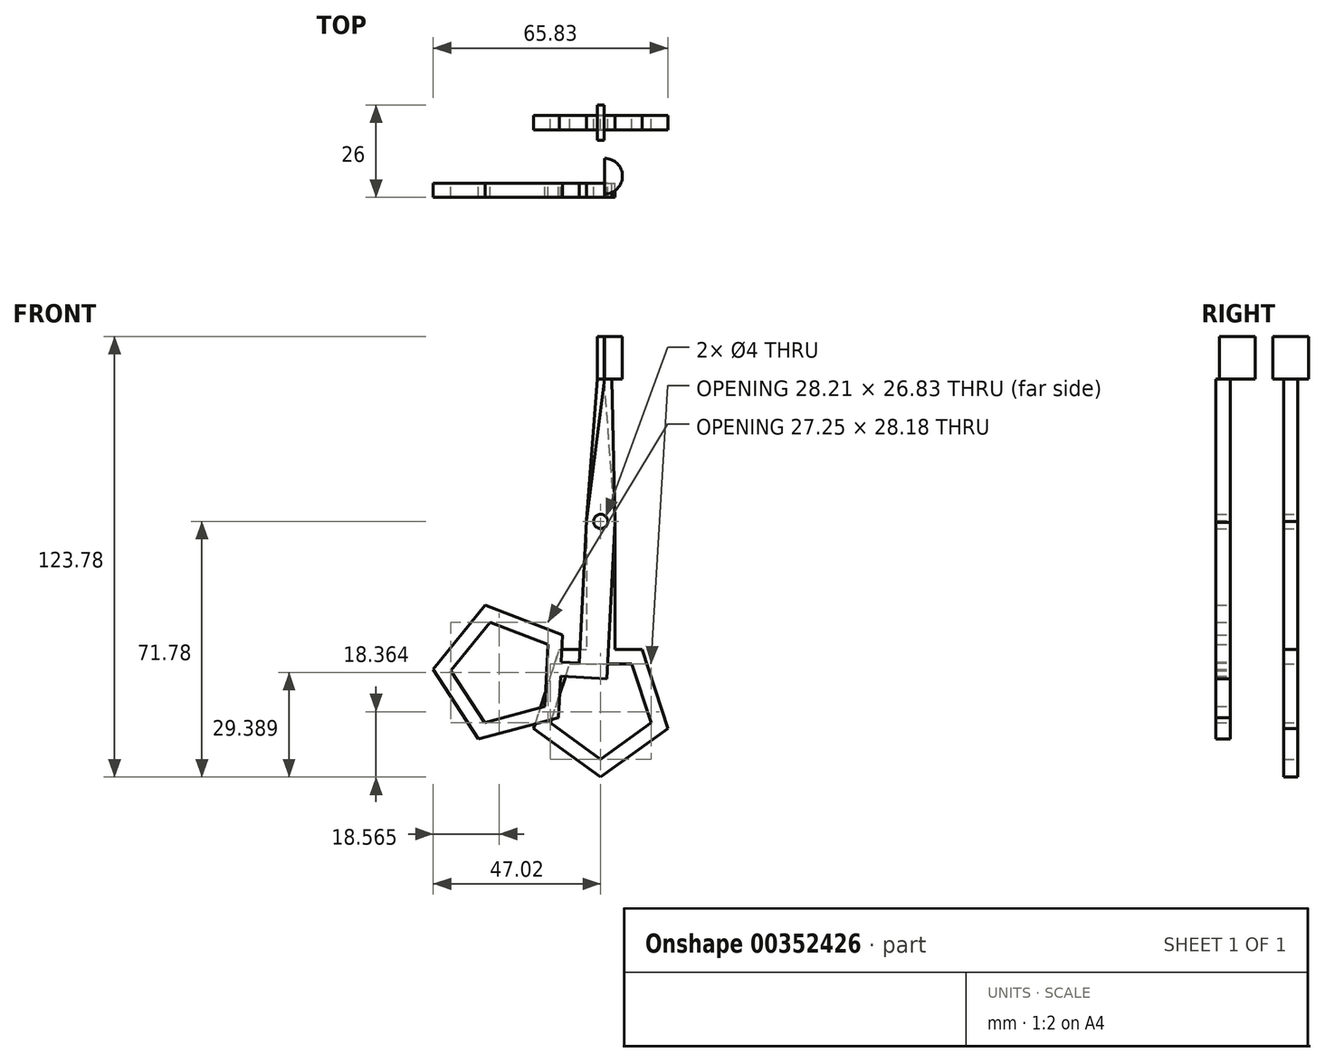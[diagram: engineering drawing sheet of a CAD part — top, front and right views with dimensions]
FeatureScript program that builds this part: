
annotation { "Feature Type Name" : "Feature", "Feature Type Description" : "" }
export const myFeature = defineFeature(function(context is Context, id is Id, definition is map)
    precondition{}
    {
        {
            var Q0;
            Q0=qCreatedBy(makeId("Front.planeOp"),FACE);
            var sketch = newSketch(context, id + "F0", { "sketchPlane" : qUnion([Q0])});
            skLineSegment(sketch, "E0.top", {"start": v(4, -40) * mm, "end": v(-4, -40) * mm});
            skLineSegment(sketch, "E0.left", {"start": v(4, 0) * mm, "end": v(4, -40) * mm});
            skLineSegment(sketch, "E0.right", {"start": v(-4, 0) * mm, "end": v(-4, -40) * mm});
            skPoint(sketch, "E0.middle", {"position": v(0, 0) * mm});
            skLineSegment(sketch, "E1", {"start": v(0, -40) * mm, "end": v(0, -52) * mm, "construction": true});
            skPoint(sketch, "E1.endSnap0", {"position": v(0, -40) * mm});
            skCircle(sketch, "E2.cCircle", {"center": v(0, -52) * mm, "radius": 12 * mm, "construction": true});
            skLineSegment(sketch, "E2.0", {"start": v(-8.72, -40) * mm, "end": v(8.72, -40) * mm});
            skLineSegment(sketch, "E2.1", {"start": v(8.72, -40) * mm, "end": v(14.1, -56.58) * mm});
            skLineSegment(sketch, "E2.2", {"start": v(14.1, -56.58) * mm, "end": v(0, -66.83) * mm});
            skLineSegment(sketch, "E2.3", {"start": v(0, -66.83) * mm, "end": v(-14.1, -56.58) * mm});
            skLineSegment(sketch, "E2.4", {"start": v(-14.1, -56.58) * mm, "end": v(-8.72, -40) * mm});
            skLineSegment(sketch, "E3", {"start": v(0, -40) * mm, "end": v(0, -36) * mm, "construction": true});
            skCircle(sketch, "E4.cCircle", {"center": v(0, -52) * mm, "radius": 16 * mm, "construction": true});
            skLineSegment(sketch, "E4.0", {"start": v(-11.62, -36) * mm, "end": v(11.62, -36) * mm});
            skLineSegment(sketch, "E4.1", {"start": v(11.62, -36) * mm, "end": v(18.8, -58.11) * mm});
            skLineSegment(sketch, "E4.2", {"start": v(18.8, -58.11) * mm, "end": v(0, -71.78) * mm});
            skLineSegment(sketch, "E4.3", {"start": v(0, -71.78) * mm, "end": v(-18.8, -58.11) * mm});
            skLineSegment(sketch, "E4.4", {"start": v(-18.8, -58.11) * mm, "end": v(-11.62, -36) * mm});
            skPoint(sketch, "E4.0.midPoint", {"position": v(0, -36) * mm});
            skLineSegment(sketch, "E5.bottom", {"start": v(-1, 40) * mm, "end": v(1, 40) * mm});
            skLineSegment(sketch, "E5.top", {"start": v(-1, 52) * mm, "end": v(1, 52) * mm});
            skLineSegment(sketch, "E5.left", {"start": v(-1, 40) * mm, "end": v(-1, 52) * mm});
            skLineSegment(sketch, "E5.right", {"start": v(1, 40) * mm, "end": v(1, 52) * mm});
            skPoint(sketch, "E6", {"position": v(0, 40) * mm});
            skCircle(sketch, "E7", {"center": v(0, 0) * mm, "radius": 2 * mm});
            skPoint(sketch, "E8", {"position": v(-4, 0) * mm});
            skPoint(sketch, "E9", {"position": v(4, 0) * mm});
            skLineSegment(sketch, "E10", {"start": v(-4, 0) * mm, "end": v(-1, 40) * mm});
            skLineSegment(sketch, "E11", {"start": v(4, 0) * mm, "end": v(1, 40) * mm});
            skSolve(sketch);
        }
        {
            var Q0;
            Q0 = qSketchRegion(id + "F0", true);
            extrude(context, id + "F1", {"entities" : qUnion([Q0]), "depth" : 4 * mm});
        }
        {
            var Q0;
            Q0=makeQuery(id+"F1.opExtrude","CAP_FACE",FACE,{"disambiguationData":[OSD([sQuery(id+"F0.wireOp",EDGE,"E0.bottom"),sQuery(id+"F0.wireOp",EDGE,"E0.left"),sQuery(id+"F0.wireOp",EDGE,"E0.right"),sQuery(id+"F0.wireOp",EDGE,"E2.0"),sQuery(id+"F0.wireOp",EDGE,"E2.1"),sQuery(id+"F0.wireOp",EDGE,"E2.2"),sQuery(id+"F0.wireOp",EDGE,"E2.3"),sQuery(id+"F0.wireOp",EDGE,"E2.4"),sQuery(id+"F0.wireOp",EDGE,"E4.0"),sQuery(id+"F0.wireOp",EDGE,"E4.1"),sQuery(id+"F0.wireOp",EDGE,"E4.2"),sQuery(id+"F0.wireOp",EDGE,"E4.3"),sQuery(id+"F0.wireOp",EDGE,"E4.4"),sQuery(id+"F0.wireOp",EDGE,"E5.top"),sQuery(id+"F0.wireOp",EDGE,"E5.left"),sQuery(id+"F0.wireOp",EDGE,"E5.right"),sQuery(id+"F0.wireOp",EDGE,"E7")])],"isStart":false});
            var sketch = newSketch(context, id + "F2", { "sketchPlane" : qUnion([Q0])});
            skLineSegment(sketch, "E12", {"start": v(-1, 40) * mm, "end": v(1, 40) * mm});
            skLineSegment(sketch, "E13", {"start": v(1, 40) * mm, "end": v(1, 52) * mm});
            skLineSegment(sketch, "E14", {"start": v(1, 52) * mm, "end": v(-1, 52) * mm});
            skLineSegment(sketch, "E15", {"start": v(-1, 52) * mm, "end": v(-1, 40) * mm});
            skSolve(sketch);
        }
        {
            var Q0;
            Q0 = qSketchRegion(id + "F2", true);
            extrude(context, id + "F3", {"entities" : qUnion([Q0]), "operationType" : NewBodyOperationType.ADD, "depth" : 3 * mm, "hasSecondDirection" : true, "secondDirectionOppositeDirection" : true, "secondDirectionDepth" : 7 * mm});
        }
        {
            var Q0;
            Q0=makeQuery(id+"F1.opExtrude","CAP_FACE",FACE,{"disambiguationData":[OSD([sQuery(id+"F0.wireOp",EDGE,"E0.left"),sQuery(id+"F0.wireOp",EDGE,"E0.right"),sQuery(id+"F0.wireOp",EDGE,"E2.0"),sQuery(id+"F0.wireOp",EDGE,"E2.1"),sQuery(id+"F0.wireOp",EDGE,"E2.2"),sQuery(id+"F0.wireOp",EDGE,"E2.3"),sQuery(id+"F0.wireOp",EDGE,"E2.4"),sQuery(id+"F0.wireOp",EDGE,"E4.0"),sQuery(id+"F0.wireOp",EDGE,"E4.1"),sQuery(id+"F0.wireOp",EDGE,"E4.2"),sQuery(id+"F0.wireOp",EDGE,"E4.3"),sQuery(id+"F0.wireOp",EDGE,"E4.4"),sQuery(id+"F0.wireOp",EDGE,"E5.top"),sQuery(id+"F0.wireOp",EDGE,"E5.left"),sQuery(id+"F0.wireOp",EDGE,"E5.right"),sQuery(id+"F0.wireOp",EDGE,"E7"),sQuery(id+"F0.wireOp",EDGE,"E10"),sQuery(id+"F0.wireOp",EDGE,"E11")])],"isStart":false});
            cPlane(context, id + "F4", {"entities" : qUnion([Q0]), "cplaneType" : CPlaneType.OFFSET, "offset" : 15 * mm, "width" : 150 * mm, "height" : 150 * mm});
        }
        {
            var Q0;
            Q0=qCreatedBy(id+"F4.planeOp",FACE);
            var sketch = newSketch(context, id + "F5", { "sketchPlane" : qUnion([Q0])});
            skLineSegment(sketch, "E16.left", {"start": v(4, -0.2) * mm, "end": v(1.9, -40.15) * mm});
            skLineSegment(sketch, "E16.right", {"start": v(-4, 0.2) * mm, "end": v(-6.09, -39.74) * mm});
            skPoint(sketch, "E16.middle", {"position": v(0, 0) * mm});
            skLineSegment(sketch, "E17.bottom", {"start": v(1.1, 40) * mm, "end": v(3.1, 39.9) * mm});
            skPoint(sketch, "E18", {"position": v(2.1, 39.95) * mm});
            skCircle(sketch, "E19", {"center": v(0, 0) * mm, "radius": 2 * mm});
            skPoint(sketch, "E20", {"position": v(-4, 0.2) * mm});
            skPoint(sketch, "E21", {"position": v(4, -0.2) * mm});
            skLineSegment(sketch, "E22", {"start": v(-4, 0.2) * mm, "end": v(1.1, 40) * mm});
            skLineSegment(sketch, "E23", {"start": v(4, -0.2) * mm, "end": v(3.1, 39.9) * mm});
            skLineSegment(sketch, "E24", {"start": v(-6.09, -39.74) * mm, "end": v(1.9, -40.15) * mm});
            skLineSegment(sketch, "E25", {"start": v(0, 0) * mm, "end": v(4, -0.2) * mm, "construction": true});
            skLineSegment(sketch, "E26", {"start": v(-4, 0.2) * mm, "end": v(0, 0) * mm, "construction": true});
            skLineSegment(sketch, "E27", {"start": v(-2, 0.1) * mm, "end": v(-4, 0.2) * mm});
            skLineSegment(sketch, "E28", {"start": v(4, -0.2) * mm, "end": v(2, -0.1) * mm});
            skLineSegment(sketch, "E29", {"start": v(-6.09, -39.74) * mm, "end": v(-15.08, -39.26) * mm});
            skLineSegment(sketch, "E30", {"start": v(-15.08, -39.26) * mm, "end": v(-15.28, -43.26) * mm});
            skLineSegment(sketch, "E31", {"start": v(-15.28, -43.26) * mm, "end": v(1.7, -44.15) * mm});
            skLineSegment(sketch, "E32", {"start": v(1.7, -44.15) * mm, "end": v(1.9, -40.15) * mm});
            skCircle(sketch, "E33.cCircle", {"center": v(-27.27, -42.63) * mm, "radius": 12 * mm, "construction": true});
            skLineSegment(sketch, "E33.0", {"start": v(-14.83, -34.55) * mm, "end": v(-15.74, -51.97) * mm});
            skLineSegment(sketch, "E33.1", {"start": v(-15.74, -51.97) * mm, "end": v(-32.58, -56.48) * mm});
            skLineSegment(sketch, "E33.2", {"start": v(-32.58, -56.48) * mm, "end": v(-42.08, -41.86) * mm});
            skLineSegment(sketch, "E33.3", {"start": v(-42.08, -41.86) * mm, "end": v(-31.1, -28.3) * mm});
            skLineSegment(sketch, "E33.4", {"start": v(-31.1, -28.3) * mm, "end": v(-14.83, -34.55) * mm});
            skPoint(sketch, "E33.0.midPoint", {"position": v(-15.28, -43.26) * mm});
            skLineSegment(sketch, "E34.0", {"start": v(-10.68, -31.86) * mm, "end": v(-11.9, -55.08) * mm});
            skLineSegment(sketch, "E34.1", {"start": v(-32.39, -23.53) * mm, "end": v(-10.68, -31.86) * mm});
            skLineSegment(sketch, "E34.2", {"start": v(-11.9, -55.08) * mm, "end": v(-34.36, -61.1) * mm});
            skLineSegment(sketch, "E34.3", {"start": v(-34.36, -61.1) * mm, "end": v(-47.02, -41.6) * mm});
            skLineSegment(sketch, "E34.4", {"start": v(-47.02, -41.6) * mm, "end": v(-32.39, -23.53) * mm});
            skLineSegment(sketch, "E35", {"start": v(1.1, 40) * mm, "end": v(3.09, 40) * mm});
            skLineSegment(sketch, "E36", {"start": v(3.09, 40) * mm, "end": v(3.1, 39.9) * mm});
            skSolve(sketch);
        }
        {
            var Q0;
            Q0 = qSketchRegion(id + "F5", true);
            extrude(context, id + "F6", {"entities" : qUnion([Q0]), "depth" : 4 * mm});
        }
        {
            var Q0;
            Q0=makeQuery(id+"F6.opExtrude","SWEPT_FACE",FACE,{"disambiguationData":[OSD([sQuery(id+"F5.wireOp",EDGE,"E35")])]});
            var sketch = newSketch(context, id + "F7", { "sketchPlane" : qUnion([Q0])});
            skLineSegment(sketch, "E37", {"start": v(1.1, -12) * mm, "end": v(1.1, -22) * mm});
            skArc(sketch, "E38", {"start": v(1.1, -22) * mm, "mid": v(6.1, -17) * mm, "end": v(1.1, -12) * mm});
            skLineSegment(sketch, "E39.0.0", {"start": v(3.09, -19) * mm, "end": v(1.1, -19) * mm});
            skLineSegment(sketch, "E39.0.1", {"start": v(1.1, -19) * mm, "end": v(1.1, -23) * mm});
            skLineSegment(sketch, "E39.0.2", {"start": v(1.1, -23) * mm, "end": v(3.09, -23) * mm});
            skLineSegment(sketch, "E39.0.3", {"start": v(3.09, -23) * mm, "end": v(3.09, -19) * mm});
            skPoint(sketch, "E40.start.orphan", {"position": v(2.1, -19) * mm});
            skLineSegment(sketch, "E41", {"start": v(1.1, -19) * mm, "end": v(1.1, -22) * mm});
            skSolve(sketch);
        }
        {
            var Q0;
            {var subQ4=sQuery(id+"F7.wireOp",EDGE,"E39.0.0");Q0=makeQuery(id+"F7.imprint","IMPRINT",FACE,{"disambiguationData":[TD([[makeQuery(id+"F7.imprint","IMPRINT",EDGE,{"derivedFrom":subQ4}),-1.0]])]});}
            var Q1;
            {var subQ0=sQuery(id+"F7.wireOp",EDGE,"E37");Q1=makeQuery(id+"F7.imprint","IMPRINT",FACE,{"disambiguationData":[TD([[makeQuery(id+"F7.imprint","IMPRINT",EDGE,{"derivedFrom":subQ0}),1.0]])]});}
            extrude(context, id + "F8", {"entities" : qUnion([Q0, Q1]), "operationType" : NewBodyOperationType.ADD, "depth" : 12 * mm});
        }
    });
